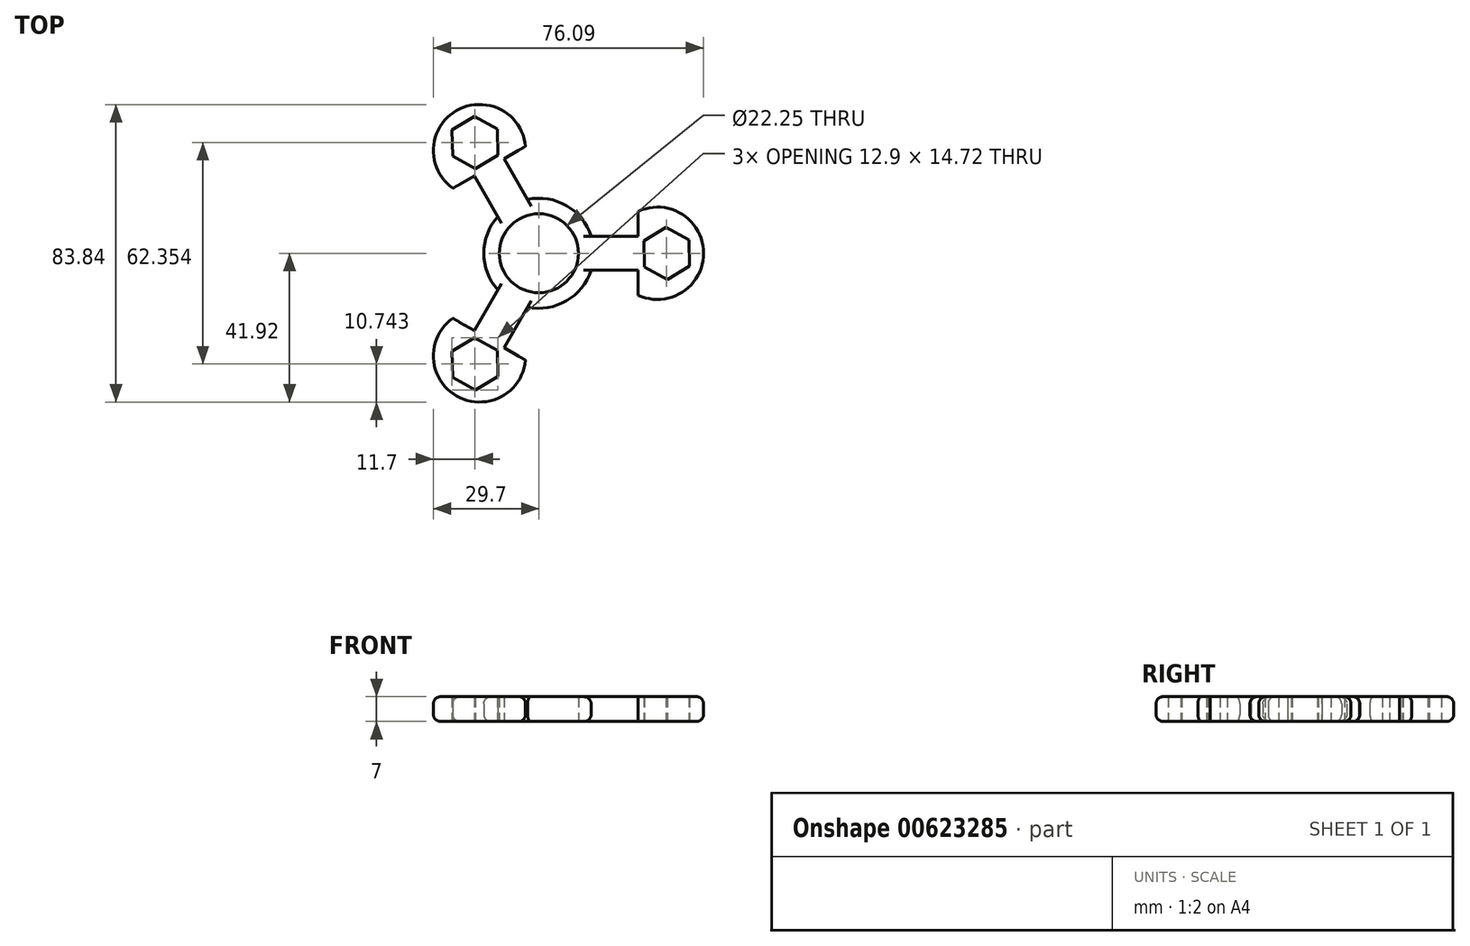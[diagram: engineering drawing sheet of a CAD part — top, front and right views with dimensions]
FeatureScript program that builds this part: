
annotation { "Feature Type Name" : "Feature", "Feature Type Description" : "" }
export const myFeature = defineFeature(function(context is Context, id is Id, definition is map)
    precondition{}
    {
        {
            var Q0;
            Q0=qCreatedBy(makeId("Top.planeOp"),FACE);
            var sketch = newSketch(context, id + "F0", { "sketchPlane" : qUnion([Q0])});
            skCircle(sketch, "E0", {"center": v(0, 0) * mm, "radius": 11.12 * mm});
            skCircle(sketch, "E1.cCircle", {"center": v(36, 0) * mm, "radius": 6.38 * mm, "construction": true});
            skLineSegment(sketch, "E1.0", {"start": v(35.85, 7.36) * mm, "end": v(42.3, 3.81) * mm});
            skLineSegment(sketch, "E1.1", {"start": v(42.3, 3.81) * mm, "end": v(42.45, -3.55) * mm});
            skLineSegment(sketch, "E1.2", {"start": v(42.45, -3.55) * mm, "end": v(36.15, -7.36) * mm});
            skLineSegment(sketch, "E1.3", {"start": v(36.15, -7.36) * mm, "end": v(29.7, -3.81) * mm});
            skLineSegment(sketch, "E1.4", {"start": v(29.7, -3.81) * mm, "end": v(29.55, 3.55) * mm});
            skLineSegment(sketch, "E1.5", {"start": v(29.55, 3.55) * mm, "end": v(35.85, 7.36) * mm});
            skPoint(sketch, "E1.0.midPoint", {"position": v(39.07, 5.58) * mm});
            skCircle(sketch, "E2", {"center": v(0, 0) * mm, "radius": 15.5 * mm});
            skPoint(sketch, "E3.first.point", {"position": v(22.02, 0) * mm});
            skPoint(sketch, "E3.second.point", {"position": v(48.01, 0) * mm});
            skPoint(sketch, "E3.third.point", {"position": v(47.08, 4.6) * mm});
            skLineSegment(sketch, "E4", {"start": v(14.73, 4.81) * mm, "end": v(27.97, 4.81) * mm});
            skCircle(sketch, "E5", {"center": v(33.4, 0) * mm, "radius": 13 * mm});
            skLineSegment(sketch, "E6", {"start": v(27.97, 4.81) * mm, "end": v(27.97, 11.82) * mm});
            skLineSegment(sketch, "E7.MirrorCS", {"start": v(14.73, -4.81) * mm, "end": v(27.97, -4.81) * mm});
            skLineSegment(sketch, "E8.MirrorCS", {"start": v(27.97, -4.81) * mm, "end": v(27.97, -11.82) * mm});
            skLineSegment(sketch, "E9.1.0", {"start": v(-17.85, 23.82) * mm, "end": v(-24.3, 27.37) * mm});
            skLineSegment(sketch, "E9.1.1", {"start": v(-24.45, 34.73) * mm, "end": v(-18.15, 38.54) * mm});
            skLineSegment(sketch, "E9.1.2", {"start": v(-18.15, 21.82) * mm, "end": v(-24.22, 18.32) * mm});
            skPoint(sketch, "E9.1.3", {"position": v(-27.52, 38.48) * mm});
            skLineSegment(sketch, "E9.1.4", {"start": v(-11.7, 34.99) * mm, "end": v(-11.55, 27.63) * mm});
            skLineSegment(sketch, "E9.1.5", {"start": v(-9.82, 26.63) * mm, "end": v(-3.75, 30.14) * mm});
            skPoint(sketch, "E9.1.6", {"position": v(-11, 19.07) * mm});
            skLineSegment(sketch, "E9.1.7", {"start": v(-11.53, 10.35) * mm, "end": v(-18.15, 21.82) * mm});
            skCircle(sketch, "E9.1.8", {"center": v(-18, 31.18) * mm, "radius": 6.38 * mm, "construction": true});
            skPoint(sketch, "E9.1.9", {"position": v(-24, 41.58) * mm});
            skPoint(sketch, "E9.1.10", {"position": v(-24.37, 31.05) * mm});
            skLineSegment(sketch, "E9.1.11", {"start": v(-18.15, 38.54) * mm, "end": v(-11.7, 34.99) * mm});
            skLineSegment(sketch, "E9.1.12", {"start": v(-11.55, 27.63) * mm, "end": v(-17.85, 23.82) * mm});
            skCircle(sketch, "E9.1.13", {"center": v(-16.7, 28.92) * mm, "radius": 13 * mm});
            skLineSegment(sketch, "E9.1.14", {"start": v(-3.2, 15.17) * mm, "end": v(-9.82, 26.63) * mm});
            skLineSegment(sketch, "E9.1.15", {"start": v(-24.3, 27.37) * mm, "end": v(-24.45, 34.73) * mm});
            skLineSegment(sketch, "E9.2.0", {"start": v(-11.7, -27.37) * mm, "end": v(-11.55, -34.73) * mm});
            skLineSegment(sketch, "E9.2.1", {"start": v(-17.85, -38.54) * mm, "end": v(-24.3, -34.99) * mm});
            skLineSegment(sketch, "E9.2.2", {"start": v(-9.82, -26.63) * mm, "end": v(-3.75, -30.14) * mm});
            skPoint(sketch, "E9.2.3", {"position": v(-19.57, -43.07) * mm});
            skLineSegment(sketch, "E9.2.4", {"start": v(-24.45, -27.63) * mm, "end": v(-18.15, -23.82) * mm});
            skLineSegment(sketch, "E9.2.5", {"start": v(-18.15, -21.82) * mm, "end": v(-24.22, -18.32) * mm});
            skPoint(sketch, "E9.2.6", {"position": v(-11, -19.07) * mm});
            skLineSegment(sketch, "E9.2.7", {"start": v(-3.2, -15.17) * mm, "end": v(-9.82, -26.63) * mm});
            skCircle(sketch, "E9.2.8", {"center": v(-18, -31.18) * mm, "radius": 6.38 * mm, "construction": true});
            skPoint(sketch, "E9.2.9", {"position": v(-24, -41.58) * mm});
            skPoint(sketch, "E9.2.10", {"position": v(-14.7, -36.63) * mm});
            skLineSegment(sketch, "E9.2.11", {"start": v(-24.3, -34.99) * mm, "end": v(-24.45, -27.63) * mm});
            skLineSegment(sketch, "E9.2.12", {"start": v(-18.15, -23.82) * mm, "end": v(-11.7, -27.37) * mm});
            skCircle(sketch, "E9.2.13", {"center": v(-16.7, -28.92) * mm, "radius": 13 * mm});
            skLineSegment(sketch, "E9.2.14", {"start": v(-11.53, -10.35) * mm, "end": v(-18.15, -21.82) * mm});
            skLineSegment(sketch, "E9.2.15", {"start": v(-11.55, -34.73) * mm, "end": v(-17.85, -38.54) * mm});
            skSolve(sketch);
        }
        {
            var Q0;
            Q0=makeQuery(id+"F0.imprint","IMPRINT",FACE,{"disambiguationData":[TD([[makeQuery(id+"F0.imprint","IMPRINT",EDGE,{"derivedFrom":sQuery(id+"F0.wireOp",EDGE,"E9.1.0")}),1.0]])]});
            var Q1;
            Q1=makeQuery(id+"F0.imprint","IMPRINT",FACE,{"disambiguationData":[TD([[makeQuery(id+"F0.imprint","IMPRINT",EDGE,{"derivedFrom":sQuery(id+"F0.wireOp",EDGE,"E1.0")}),1.0]])]});
            var Q2;
            Q2=makeQuery(id+"F0.imprint","IMPRINT",FACE,{"disambiguationData":[TD([[makeQuery(id+"F0.imprint","IMPRINT",EDGE,{"derivedFrom":sQuery(id+"F0.wireOp",EDGE,"E9.2.0")}),1.0]])]});
            var Q3;
            Q3=makeQuery(id+"F0.imprint","IMPRINT",FACE,{"disambiguationData":[TD([[makeQuery(id+"F0.imprint","IMPRINT",EDGE,{"derivedFrom":sQuery(id+"F0.wireOp",EDGE,"E0")}),-1.0]])]});
            var Q4;
            {var subQ0=sQuery(id+"F0.wireOp",EDGE,"E9.2.7");var subQ1=sQuery(id+"F0.wireOp",EDGE,"E2");var subQ2=makeQuery(id+"F0.imprint","INTERSECT",VERTEX,{"derivedFrom":[subQ1,subQ0]});Q4=makeQuery(id+"F0.imprint","IMPRINT",FACE,{"disambiguationData":[TD([[makeQuery(id+"F0.imprint","IMPRINT",EDGE,{"disambiguationData":[TD([[subQ2,1.0]])],"derivedFrom":subQ1}),-1.0]])]});}
            var Q5;
            {var subQ0=sQuery(id+"F0.wireOp",EDGE,"E4");var subQ1=sQuery(id+"F0.wireOp",EDGE,"E2");var subQ2=makeQuery(id+"F0.imprint","INTERSECT",VERTEX,{"derivedFrom":[subQ1,subQ0]});Q5=makeQuery(id+"F0.imprint","IMPRINT",FACE,{"disambiguationData":[TD([[makeQuery(id+"F0.imprint","IMPRINT",EDGE,{"disambiguationData":[TD([[subQ2,1.0]])],"derivedFrom":subQ1}),-1.0]])]});}
            var Q6;
            {var subQ0=sQuery(id+"F0.wireOp",EDGE,"E9.1.7");var subQ1=sQuery(id+"F0.wireOp",EDGE,"E2");var subQ2=makeQuery(id+"F0.imprint","INTERSECT",VERTEX,{"derivedFrom":[subQ1,subQ0]});Q6=makeQuery(id+"F0.imprint","IMPRINT",FACE,{"disambiguationData":[TD([[makeQuery(id+"F0.imprint","IMPRINT",EDGE,{"disambiguationData":[TD([[subQ2,1.0]])],"derivedFrom":subQ1}),-1.0]])]});}
            extrude(context, id + "F1", {"entities" : qUnion([Q0, Q1, Q2, Q3, Q4, Q5, Q6]), "depth" : 7 * mm, "offsetDistance" : 25 * mm});
        }
        {
            var Q0;
            Q0=makeQuery(id+"F1.opExtrude","CAP_EDGE",EDGE,{"disambiguationData":[OSD([sQuery(id+"F0.wireOp",EDGE,"E5")])],"isStart":false});
            var Q1;
            Q1=makeQuery(id+"F1.opExtrude","CAP_EDGE",EDGE,{"disambiguationData":[OSD([sQuery(id+"F0.wireOp",EDGE,"E5")])],"isStart":true});
            var Q2;
            Q2=makeQuery(id+"F1.opExtrude","CAP_EDGE",EDGE,{"disambiguationData":[OSD([sQuery(id+"F0.wireOp",EDGE,"E9.2.13")])],"isStart":true});
            var Q3;
            Q3=makeQuery(id+"F1.opExtrude","CAP_EDGE",EDGE,{"disambiguationData":[OSD([sQuery(id+"F0.wireOp",EDGE,"E9.2.13")])],"isStart":false});
            var Q4;
            Q4=makeQuery(id+"F1.opExtrude","CAP_EDGE",EDGE,{"disambiguationData":[OSD([sQuery(id+"F0.wireOp",EDGE,"E9.1.13")])],"isStart":false});
            var Q5;
            Q5=makeQuery(id+"F1.opExtrude","CAP_EDGE",EDGE,{"disambiguationData":[OSD([sQuery(id+"F0.wireOp",EDGE,"E9.1.13")])],"isStart":true});
            var Q6;
            {var subQ0=sQuery(id+"F0.wireOp",EDGE,"E2");Q6=makeQuery(id+"F1.opExtrude","CAP_EDGE",EDGE,{"disambiguationData":[OSD([subQ0]),TDD([makeQuery(id+"F0.imprint","IMPRINT",EDGE,{"disambiguationData":[TD([[makeQuery(id+"F0.imprint","INTERSECT",VERTEX,{"derivedFrom":[subQ0,sQuery(id+"F0.wireOp",EDGE,"E7.MirrorCS")]}),1.0]])],"derivedFrom":subQ0})])],"isStart":true});}
            var Q7;
            {var subQ0=sQuery(id+"F0.wireOp",EDGE,"E2");Q7=makeQuery(id+"F1.opExtrude","CAP_EDGE",EDGE,{"disambiguationData":[OSD([subQ0]),TDD([makeQuery(id+"F0.imprint","IMPRINT",EDGE,{"disambiguationData":[TD([[makeQuery(id+"F0.imprint","INTERSECT",VERTEX,{"derivedFrom":[subQ0,sQuery(id+"F0.wireOp",EDGE,"E9.1.7")]}),-1.0]])],"derivedFrom":subQ0})])],"isStart":true});}
            var Q8;
            {var subQ0=sQuery(id+"F0.wireOp",EDGE,"E2");Q8=makeQuery(id+"F1.opExtrude","CAP_EDGE",EDGE,{"disambiguationData":[OSD([subQ0]),TDD([makeQuery(id+"F0.imprint","IMPRINT",EDGE,{"disambiguationData":[TD([[makeQuery(id+"F0.imprint","INTERSECT",VERTEX,{"derivedFrom":[subQ0,sQuery(id+"F0.wireOp",EDGE,"E4")]}),-1.0]])],"derivedFrom":subQ0})])],"isStart":true});}
            var Q9;
            {var subQ0=sQuery(id+"F0.wireOp",EDGE,"E2");Q9=makeQuery(id+"F1.opExtrude","CAP_EDGE",EDGE,{"disambiguationData":[OSD([subQ0]),TDD([makeQuery(id+"F0.imprint","IMPRINT",EDGE,{"disambiguationData":[TD([[makeQuery(id+"F0.imprint","INTERSECT",VERTEX,{"derivedFrom":[subQ0,sQuery(id+"F0.wireOp",EDGE,"E4")]}),-1.0]])],"derivedFrom":subQ0})])],"isStart":false});}
            var Q10;
            {var subQ0=sQuery(id+"F0.wireOp",EDGE,"E2");Q10=makeQuery(id+"F1.opExtrude","CAP_EDGE",EDGE,{"disambiguationData":[OSD([subQ0]),TDD([makeQuery(id+"F0.imprint","IMPRINT",EDGE,{"disambiguationData":[TD([[makeQuery(id+"F0.imprint","INTERSECT",VERTEX,{"derivedFrom":[subQ0,sQuery(id+"F0.wireOp",EDGE,"E7.MirrorCS")]}),1.0]])],"derivedFrom":subQ0})])],"isStart":false});}
            var Q11;
            {var subQ0=sQuery(id+"F0.wireOp",EDGE,"E2");Q11=makeQuery(id+"F1.opExtrude","CAP_EDGE",EDGE,{"disambiguationData":[OSD([subQ0]),TDD([makeQuery(id+"F0.imprint","IMPRINT",EDGE,{"disambiguationData":[TD([[makeQuery(id+"F0.imprint","INTERSECT",VERTEX,{"derivedFrom":[subQ0,sQuery(id+"F0.wireOp",EDGE,"E9.1.7")]}),-1.0]])],"derivedFrom":subQ0})])],"isStart":false});}
            fillet(context, id + "F2", {"entities" : qUnion([Q0, Q1, Q2, Q3, Q4, Q5, Q6, Q7, Q8, Q9, Q10, Q11]), "radius" : 2 * mm, "tangentPropagation" : true, "allowEdgeOverflow" : false});
        }
    });
